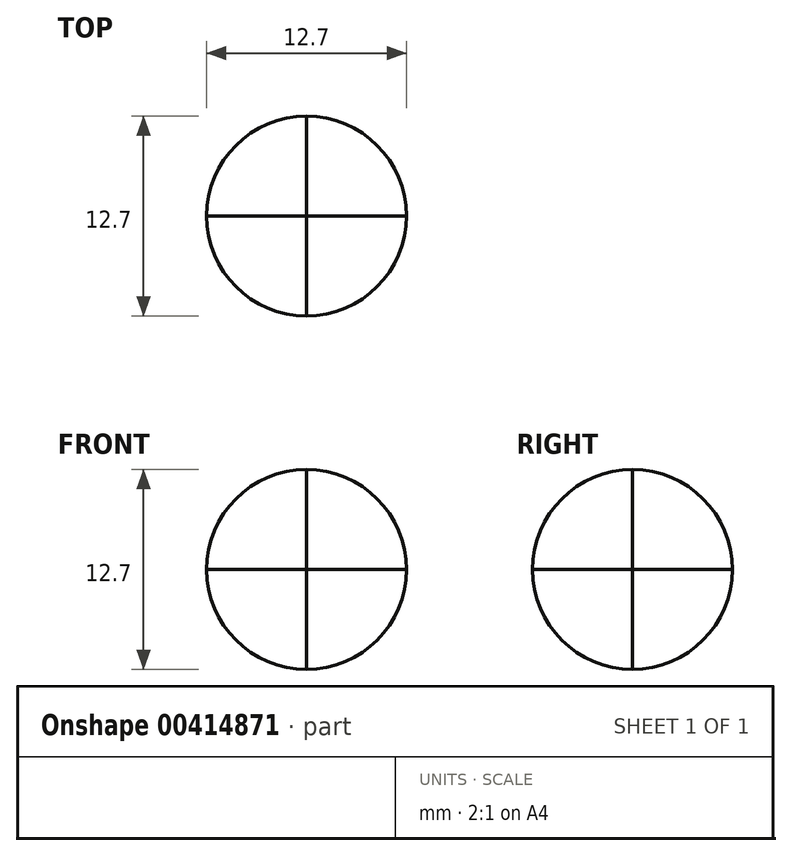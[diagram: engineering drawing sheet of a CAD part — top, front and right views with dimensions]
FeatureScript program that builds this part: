
annotation { "Feature Type Name" : "Feature", "Feature Type Description" : "" }
export const myFeature = defineFeature(function(context is Context, id is Id, definition is map)
    precondition{}
    {
        {
            var Q0;
            Q0=qCreatedBy(makeId("Front.planeOp"),FACE);
            var sketch = newSketch(context, id + "F0", { "sketchPlane" : qUnion([Q0])});
            skCircle(sketch, "E0", {"center": v(0, 0) * mm, "radius": 6.35 * mm});
            skSolve(sketch);
        }
        {
            var Q0;
            Q0=qSketchRegion(id+"F0",true);
            extrude(context, id + "F1", {"entities" : qUnion([Q0]), "oppositeDirection" : true, "depth" : 0 * mm});
        }
        {
            var Q0;
            Q0=qCreatedBy(makeId("Right.planeOp"),FACE);
            var sketch = newSketch(context, id + "F2", { "sketchPlane" : qUnion([Q0])});
            skCircle(sketch, "E1", {"center": v(0, 0) * mm, "radius": 6.35 * mm});
            skSolve(sketch);
        }
        {
            var Q0;
            Q0=qSketchRegion(id+"F2",true);
            extrude(context, id + "F3", {"entities" : qUnion([Q0]), "operationType" : NewBodyOperationType.ADD, "oppositeDirection" : true, "depth" : 0 * mm});
        }
        {
            var Q0;
            Q0=qCreatedBy(makeId("Top.planeOp"),FACE);
            var sketch = newSketch(context, id + "F4", { "sketchPlane" : qUnion([Q0])});
            skCircle(sketch, "E2", {"center": v(0, 0) * mm, "radius": 6.35 * mm});
            skSolve(sketch);
        }
        {
            var Q0;
            Q0=qSketchRegion(id+"F4",true);
            extrude(context, id + "F5", {"entities" : qUnion([Q0]), "operationType" : NewBodyOperationType.ADD, "oppositeDirection" : true, "depth" : 0 * mm});
        }
    });
